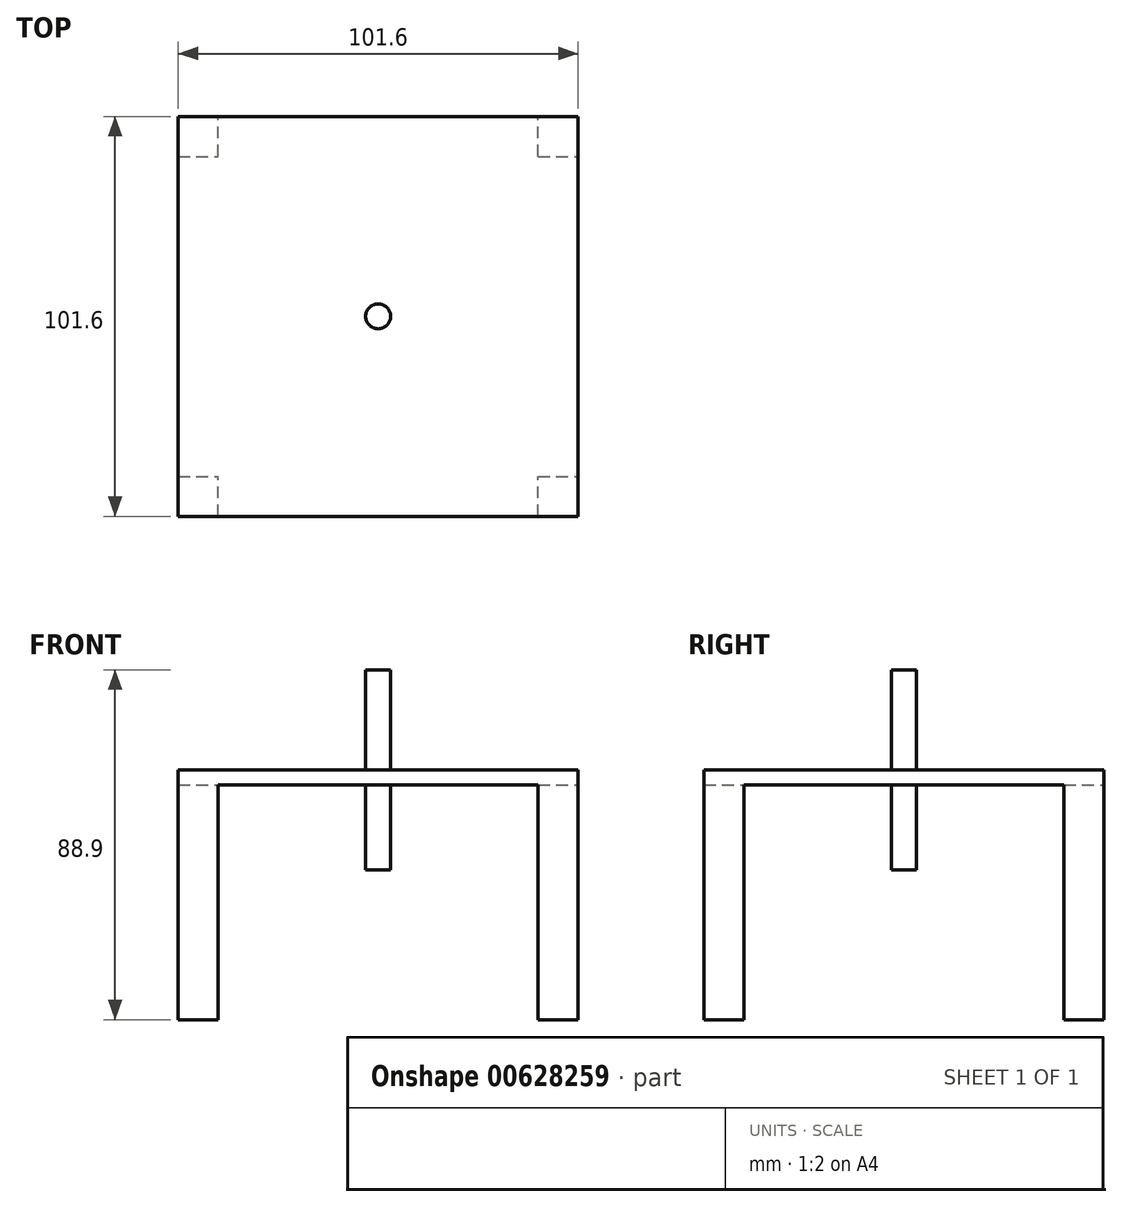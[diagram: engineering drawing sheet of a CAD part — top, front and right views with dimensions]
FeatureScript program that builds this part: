
annotation { "Feature Type Name" : "Feature", "Feature Type Description" : "" }
export const myFeature = defineFeature(function(context is Context, id is Id, definition is map)
    precondition{}
    {
        {
            var Q0;
            Q0=qCreatedBy(makeId("Top.planeOp"),FACE);
            var sketch = newSketch(context, id + "F0", { "sketchPlane" : qUnion([Q0])});
            skLineSegment(sketch, "E0.bottom", {"start": v(0, 0) * mm, "end": v(-101.6, 0) * mm});
            skLineSegment(sketch, "E0.top", {"start": v(0, -101.6) * mm, "end": v(-101.6, -101.6) * mm});
            skLineSegment(sketch, "E0.left", {"start": v(0, 0) * mm, "end": v(0, -101.6) * mm});
            skLineSegment(sketch, "E0.right", {"start": v(-101.6, 0) * mm, "end": v(-101.6, -101.6) * mm});
            skSolve(sketch);
        }
        {
            var Q0;
            Q0=qSketchRegion(id+"F0",true);
            extrude(context, id + "F1", {"entities" : qUnion([Q0]), "depth" : 63.5 * mm, "offsetDistance" : 25.4 * mm});
        }
        {
            var Q0;
            Q0=makeQuery(id+"F1.opExtrude","CAP_FACE",FACE,{"disambiguationData":[OSD([sQuery(id+"F0.wireOp",EDGE,"E0.bottom"),sQuery(id+"F0.wireOp",EDGE,"E0.top"),sQuery(id+"F0.wireOp",EDGE,"E0.left"),sQuery(id+"F0.wireOp",EDGE,"E0.right")])],"isStart":true});
            var sketch = newSketch(context, id + "F2", { "sketchPlane" : qUnion([Q0])});
            skLineSegment(sketch, "E1.bottom", {"start": v(-110.14, 91.44) * mm, "end": v(13.73, 91.44) * mm});
            skLineSegment(sketch, "E1.top", {"start": v(-110.14, 10.16) * mm, "end": v(13.73, 10.16) * mm});
            skLineSegment(sketch, "E1.left", {"start": v(-110.14, 91.44) * mm, "end": v(-110.14, 10.16) * mm});
            skLineSegment(sketch, "E1.right", {"start": v(13.73, 91.44) * mm, "end": v(13.73, 10.16) * mm});
            skLineSegment(sketch, "E2", {"start": v(-138.08, 101.6) * mm, "end": v(53.38, 101.6) * mm, "construction": true});
            skLineSegment(sketch, "E3", {"start": v(-147.77, 0) * mm, "end": v(62.75, 0) * mm, "construction": true});
            skLineSegment(sketch, "E4.bottom", {"start": v(-91.44, 115.57) * mm, "end": v(-10.16, 115.57) * mm});
            skLineSegment(sketch, "E4.top", {"start": v(-91.44, -18.63) * mm, "end": v(-10.16, -18.63) * mm});
            skLineSegment(sketch, "E4.left", {"start": v(-91.44, 115.57) * mm, "end": v(-91.44, -18.63) * mm});
            skLineSegment(sketch, "E4.right", {"start": v(-10.16, 115.57) * mm, "end": v(-10.16, -18.63) * mm});
            skSolve(sketch);
        }
        {
            var Q0;
            {var subQ0=sQuery(id+"F2.wireOp",EDGE,"E4.left");var subQ1=sQuery(id+"F2.wireOp",EDGE,"E1.bottom");var subQ2=makeQuery(id+"F2.imprint","INTERSECT",VERTEX,{"derivedFrom":[subQ1,subQ0]});Q0=makeQuery(id+"F2.imprint","IMPRINT",FACE,{"disambiguationData":[TD([[makeQuery(id+"F2.imprint","IMPRINT",EDGE,{"disambiguationData":[TD([[subQ2,-1.0]])],"derivedFrom":subQ1}),-1.0]])]});}
            var Q1;
            {var subQ0=sQuery(id+"F2.wireOp",EDGE,"E4.right");var subQ1=sQuery(id+"F2.wireOp",EDGE,"E1.bottom");var subQ2=makeQuery(id+"F2.imprint","INTERSECT",VERTEX,{"derivedFrom":[subQ1,subQ0]});Q1=makeQuery(id+"F2.imprint","IMPRINT",FACE,{"disambiguationData":[TD([[makeQuery(id+"F2.imprint","IMPRINT",EDGE,{"disambiguationData":[TD([[subQ2,-1.0]])],"derivedFrom":subQ1}),-1.0]])]});}
            var Q2;
            {var subQ0=sQuery(id+"F2.wireOp",EDGE,"E4.left");var subQ1=sQuery(id+"F2.wireOp",EDGE,"E1.top");var subQ2=makeQuery(id+"F2.imprint","INTERSECT",VERTEX,{"derivedFrom":[subQ1,subQ0]});Q2=makeQuery(id+"F2.imprint","IMPRINT",FACE,{"disambiguationData":[TD([[makeQuery(id+"F2.imprint","IMPRINT",EDGE,{"disambiguationData":[TD([[subQ2,-1.0]])],"derivedFrom":subQ1}),-1.0]])]});}
            var Q3;
            {var subQ0=sQuery(id+"F2.wireOp",EDGE,"E4.left");var subQ1=sQuery(id+"F2.wireOp",EDGE,"E1.bottom");var subQ2=makeQuery(id+"F2.imprint","INTERSECT",VERTEX,{"derivedFrom":[subQ1,subQ0]});Q3=makeQuery(id+"F2.imprint","IMPRINT",FACE,{"disambiguationData":[TD([[makeQuery(id+"F2.imprint","IMPRINT",EDGE,{"disambiguationData":[TD([[subQ2,1.0]])],"derivedFrom":subQ1}),-1.0]])]});}
            var Q4;
            {var subQ0=sQuery(id+"F2.wireOp",EDGE,"E4.left");var subQ1=sQuery(id+"F2.wireOp",EDGE,"E1.bottom");var subQ2=makeQuery(id+"F2.imprint","INTERSECT",VERTEX,{"derivedFrom":[subQ1,subQ0]});Q4=makeQuery(id+"F2.imprint","IMPRINT",FACE,{"disambiguationData":[TD([[makeQuery(id+"F2.imprint","IMPRINT",EDGE,{"disambiguationData":[TD([[subQ2,-1.0]])],"derivedFrom":subQ1}),1.0]])]});}
            extrude(context, id + "F3", {"entities" : qUnion([Q0, Q1, Q2, Q3, Q4]), "operationType" : NewBodyOperationType.REMOVE, "oppositeDirection" : true, "depth" : 59.69 * mm, "offsetDistance" : 25.4 * mm});
        }
        {
            var Q0;
            Q0=makeQuery(id+"F1.opExtrude","CAP_FACE",FACE,{"disambiguationData":[OSD([sQuery(id+"F0.wireOp",EDGE,"E0.bottom"),sQuery(id+"F0.wireOp",EDGE,"E0.top"),sQuery(id+"F0.wireOp",EDGE,"E0.left"),sQuery(id+"F0.wireOp",EDGE,"E0.right")])],"isStart":false});
            var sketch = newSketch(context, id + "F4", { "sketchPlane" : qUnion([Q0])});
            skLineSegment(sketch, "E5", {"start": v(-101.6, 0) * mm, "end": v(0, -101.6) * mm});
            skCircle(sketch, "E6", {"center": v(-50.8, -50.8) * mm, "radius": 3.17 * mm});
            skSolve(sketch);
        }
        {
            var Q0;
            {var subQ0=sQuery(id+"F4.wireOp",EDGE,"E6");var subQ1=sQuery(id+"F4.wireOp",EDGE,"E5");var subQ2=makeQuery(id+"F4.imprint","INTERSECT",VERTEX,{"disambiguationData":[OD(0.0)],"derivedFrom":[subQ1,subQ0]});Q0=makeQuery(id+"F4.imprint","IMPRINT",FACE,{"disambiguationData":[TD([[makeQuery(id+"F4.imprint","IMPRINT",EDGE,{"disambiguationData":[TD([[subQ2,-1.0]])],"derivedFrom":subQ1}),1.0]])]});}
            var Q1;
            {var subQ0=sQuery(id+"F4.wireOp",EDGE,"E6");var subQ1=sQuery(id+"F4.wireOp",EDGE,"E5");var subQ2=makeQuery(id+"F4.imprint","INTERSECT",VERTEX,{"disambiguationData":[OD(0.0)],"derivedFrom":[subQ1,subQ0]});Q1=makeQuery(id+"F4.imprint","IMPRINT",FACE,{"disambiguationData":[TD([[makeQuery(id+"F4.imprint","IMPRINT",EDGE,{"disambiguationData":[TD([[subQ2,-1.0]])],"derivedFrom":subQ1}),-1.0]])]});}
            extrude(context, id + "F5", {"entities" : qUnion([Q0, Q1]), "operationType" : NewBodyOperationType.REMOVE, "endBound" : BoundingType.THROUGH_ALL, "oppositeDirection" : true, "depth" : 25.4 * mm, "offsetDistance" : 25.4 * mm});
        }
        {
            var Q0;
            Q0=makeQuery(id+"F1.opExtrude","CAP_FACE",FACE,{"disambiguationData":[OSD([sQuery(id+"F0.wireOp",EDGE,"E0.bottom"),sQuery(id+"F0.wireOp",EDGE,"E0.top"),sQuery(id+"F0.wireOp",EDGE,"E0.left"),sQuery(id+"F0.wireOp",EDGE,"E0.right")])],"isStart":false});
            var sketch = newSketch(context, id + "F6", { "sketchPlane" : qUnion([Q0])});
            skCircle(sketch, "E7", {"center": v(-50.8, -50.8) * mm, "radius": 3.18 * mm});
            skSolve(sketch);
        }
        {
            var Q0;
            Q0=makeQuery(id+"F6.imprint","IMPRINT",FACE,{"disambiguationData":[TD([[makeQuery(id+"F6.imprint","IMPRINT",EDGE,{"derivedFrom":sQuery(id+"F6.wireOp",EDGE,"E7")}),1.0]])]});
            extrude(context, id + "F7", {"entities" : qUnion([Q0]), "operationType" : NewBodyOperationType.ADD, "endBound" : BoundingType.SYMMETRIC, "depth" : 50.8 * mm, "offsetDistance" : 25.4 * mm});
        }
    });
